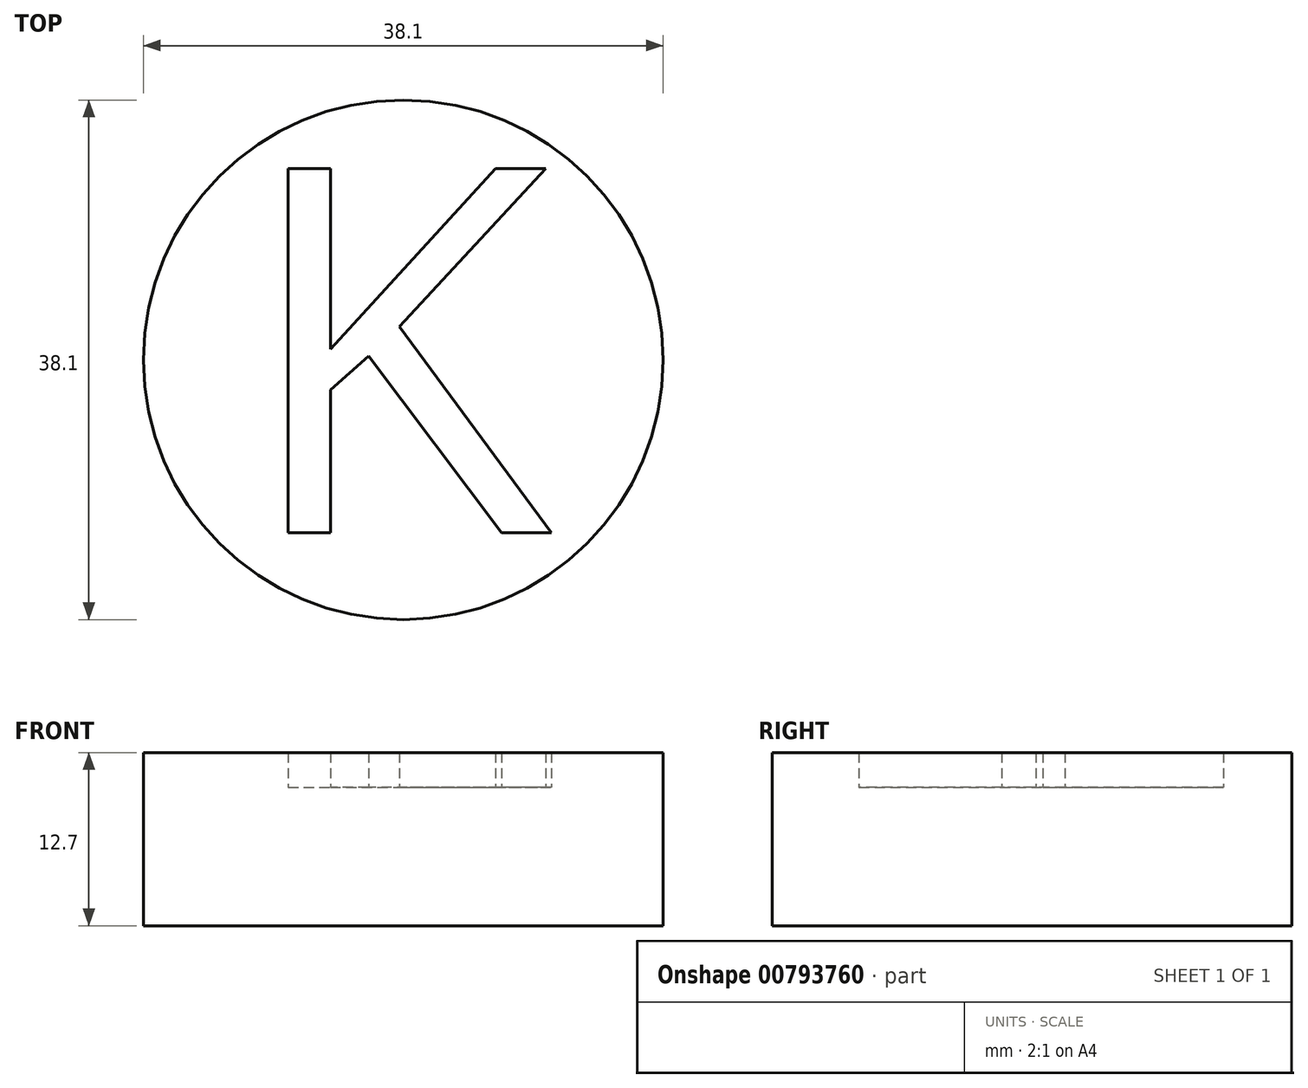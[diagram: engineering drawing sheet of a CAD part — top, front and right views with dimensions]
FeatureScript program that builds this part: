
annotation { "Feature Type Name" : "Feature", "Feature Type Description" : "" }
export const myFeature = defineFeature(function(context is Context, id is Id, definition is map)
    precondition{}
    {
        {
            var Q0;
            Q0=qCreatedBy(makeId("Top.planeOp"),FACE);
            var sketch = newSketch(context, id + "F0", { "sketchPlane" : qUnion([Q0])});
            skCircle(sketch, "E0", {"center": v(0, 0) * mm, "radius": 19.05 * mm});
            skSolve(sketch);
        }
        {
            var Q0;
            Q0 = qSketchRegion(id + "F0", true);
            extrude(context, id + "F1", {"entities" : qUnion([Q0]), "depth" : 12.7 * mm, "offsetDistance" : 25.4 * mm});
        }
        {
            var Q0;
            Q0=qCreatedBy(makeId("Top.planeOp"),FACE);
            var sketch = newSketch(context, id + "F2", { "sketchPlane" : qUnion([Q0])});
            skText(sketch, "E1", { "text": "K", "fontName": "OpenSans-Regular.ttf"});
            const initialGuessF2  = {"E1": [-0.01212, -0.01269, 1, 0, 0.02695]};
            skSetInitialGuess(sketch, initialGuessF2);
            skSolve(sketch);
        }
        {
            var Q0;
            Q0 = qSketchRegion(id + "F2", true);
            extrude(context, id + "F3", {"entities" : qUnion([Q0]), "operationType" : NewBodyOperationType.REMOVE, "depth" : 12.7 * mm, "offsetDistance" : 25.4 * mm, "hasSecondDirection" : true, "secondDirectionOppositeDirection" : false, "secondDirectionDepth" : 10.16 * mm});
        }
    });
